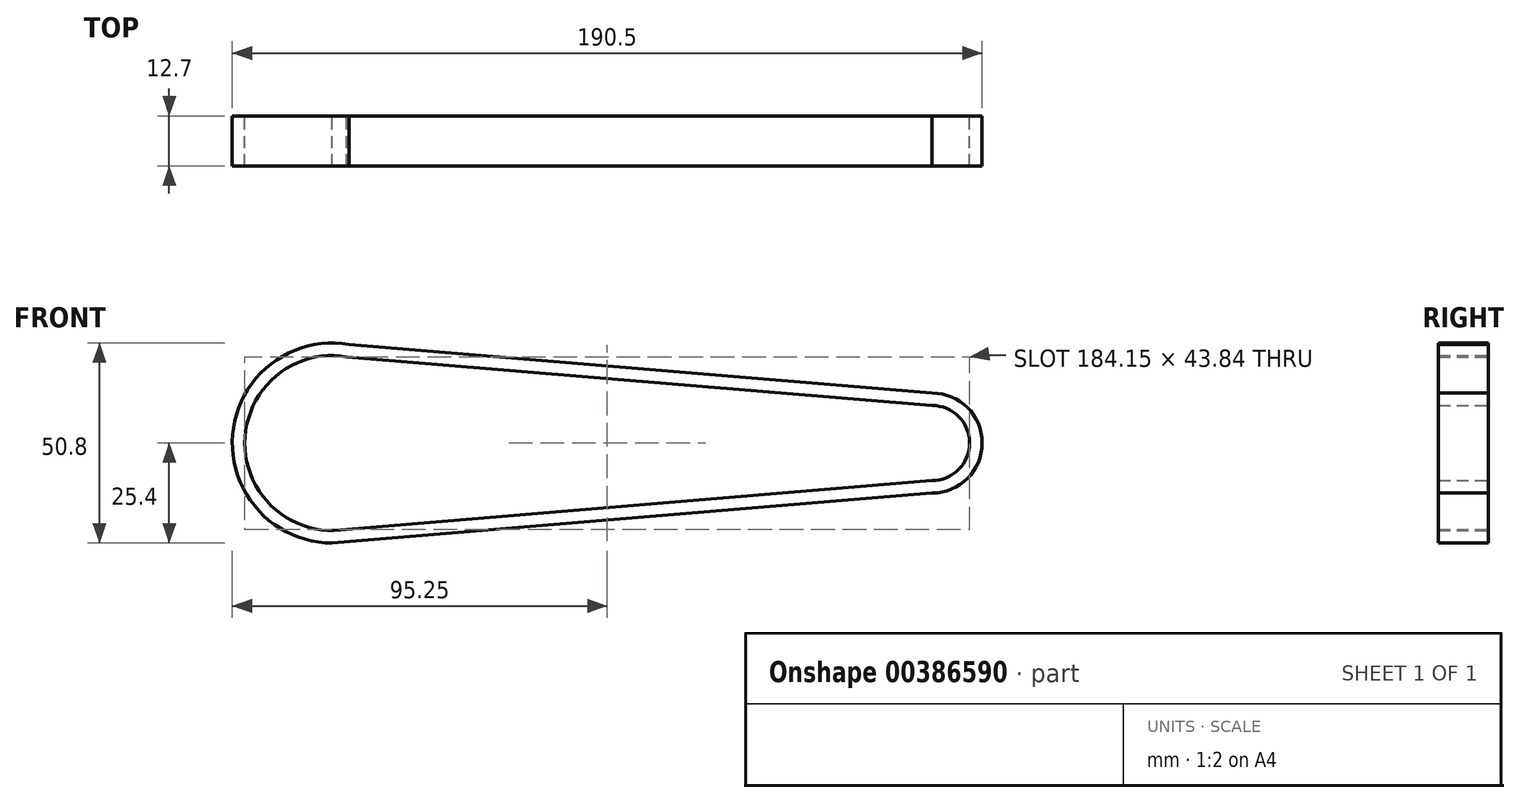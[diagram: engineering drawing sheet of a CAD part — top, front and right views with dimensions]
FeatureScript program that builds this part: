
annotation { "Feature Type Name" : "Feature", "Feature Type Description" : "" }
export const myFeature = defineFeature(function(context is Context, id is Id, definition is map)
    precondition{}
    {
        {
            var Q0;
            Q0=qCreatedBy(makeId("Front.planeOp"),FACE);
            var sketch = newSketch(context, id + "F0", { "sketchPlane" : qUnion([Q0])});
            skArc(sketch, "E0", {"start": v(3.68, 21.92) * mm, "mid": v(-22.22, 0) * mm, "end": v(3.68, -21.92) * mm});
            skArc(sketch, "E1", {"start": v(152.4, -9.52) * mm, "mid": v(161.93, 0) * mm, "end": v(152.4, 9.53) * mm});
            skLineSegment(sketch, "E2", {"start": v(0, -22.22) * mm, "end": v(152.4, -9.53) * mm});
            skLineSegment(sketch, "E3", {"start": v(0, 22.22) * mm, "end": v(152.4, 9.53) * mm});
            skArc(sketch, "E4", {"start": v(4.2, 25.05) * mm, "mid": v(-25.31, 2.1) * mm, "end": v(0, -25.4) * mm});
            skArc(sketch, "E5", {"start": v(152.4, -12.7) * mm, "mid": v(165.1, 0) * mm, "end": v(152.4, 12.7) * mm});
            skLineSegment(sketch, "E6", {"start": v(0, 25.4) * mm, "end": v(152.4, 12.7) * mm});
            skLineSegment(sketch, "E7", {"start": v(0, -25.4) * mm, "end": v(152.4, -12.7) * mm});
            skSolve(sketch);
        }
        {
            var Q0;
            Q0 = qSketchRegion(id + "F0", true);
            extrude(context, id + "F1", {"entities" : qUnion([Q0]), "depth" : 12.7 * mm});
        }
    });
